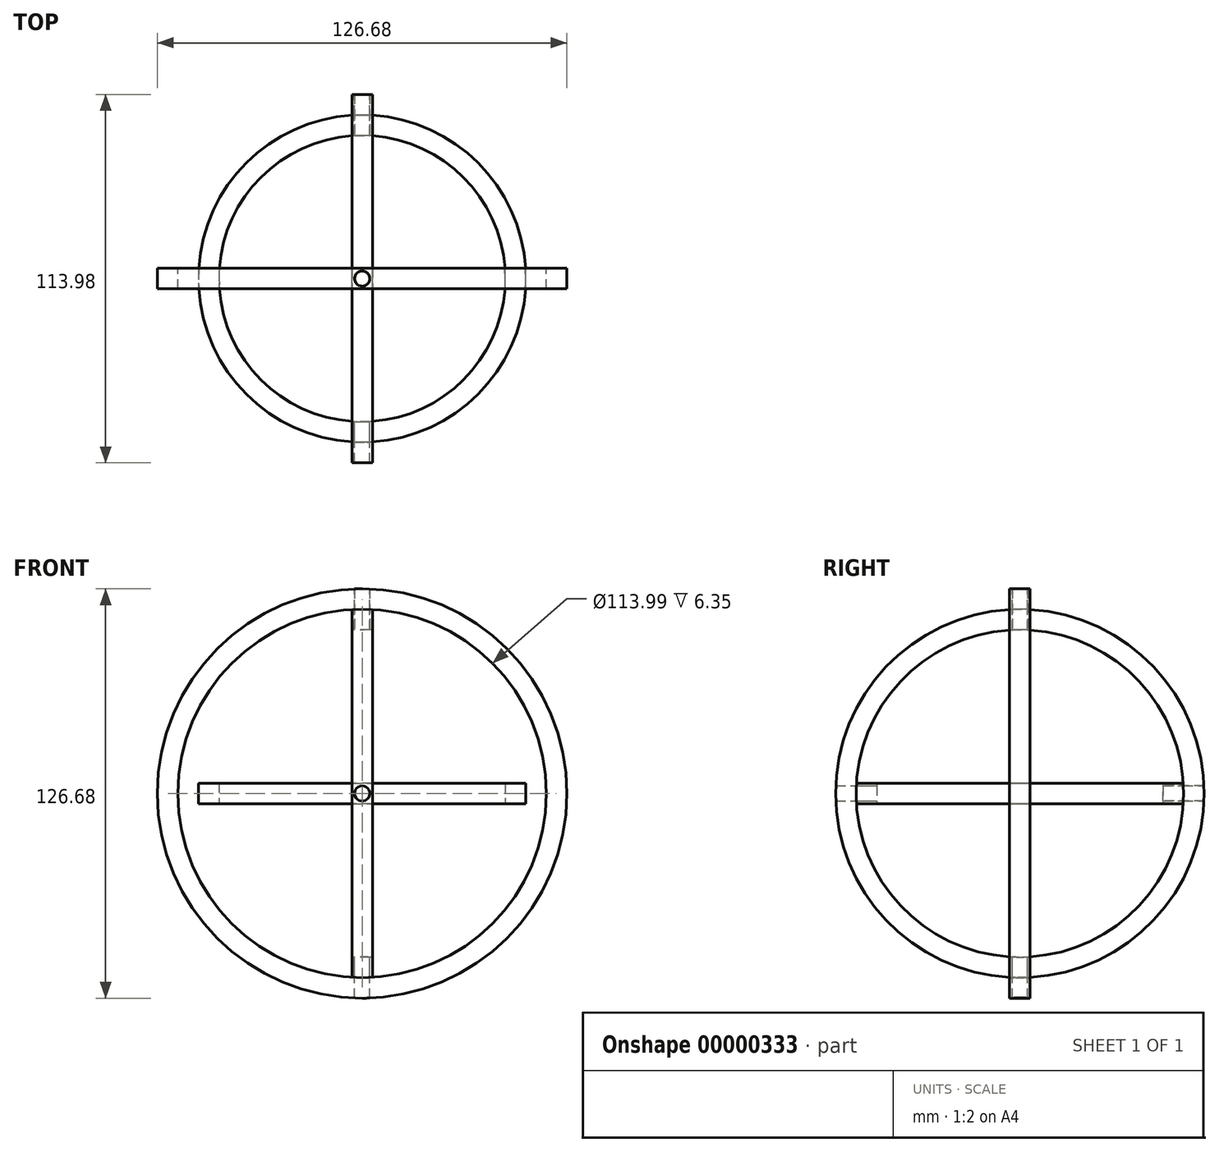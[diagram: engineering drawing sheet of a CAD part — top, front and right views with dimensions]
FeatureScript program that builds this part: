
annotation { "Feature Type Name" : "Feature", "Feature Type Description" : "" }
export const myFeature = defineFeature(function(context is Context, id is Id, definition is map)
    precondition{}
    {
        {
            var Q0;
            Q0=qCreatedBy(makeId("Top.planeOp"),FACE);
            var sketch = newSketch(context, id + "F0", { "sketchPlane" : qUnion([Q0])});
            skCircle(sketch, "E0", {"center": v(0, 0) * mm, "radius": 50.64 * mm});
            skCircle(sketch, "E1", {"center": v(0, 0) * mm, "radius": 44.3 * mm});
            skLineSegment(sketch, "E2", {"start": v(-44.3, 0) * mm, "end": v(-50.64, 0) * mm, "construction": true});
            skLineSegment(sketch, "E3", {"start": v(0, 50.64) * mm, "end": v(0, -50.64) * mm, "construction": true});
            skSolve(sketch);
        }
        {
            var Q0;
            Q0=makeQuery(id+"F0.imprint","IMPRINT",FACE,{"disambiguationData":[TD([[makeQuery(id+"F0.imprint","IMPRINT",EDGE,{"derivedFrom":sQuery(id+"F0.wireOp",EDGE,"E0")}),1.0]])]});
            extrude(context, id + "F1", {"entities" : qUnion([Q0]), "depth" : 3.17 * mm, "hasSecondDirection" : true, "secondDirectionOppositeDirection" : true, "secondDirectionDepth" : 3.17 * mm});
        }
        {
            var Q0;
            Q0=qCreatedBy(makeId("Right.planeOp"),FACE);
            var sketch = newSketch(context, id + "F2", { "sketchPlane" : qUnion([Q0])});
            skPoint(sketch, "E4.0", {"position": v(50.64, 0) * mm});
            skCircle(sketch, "E5", {"center": v(0, 0) * mm, "radius": 50.64 * mm});
            skCircle(sketch, "E6", {"center": v(0, 0) * mm, "radius": 57 * mm});
            skLineSegment(sketch, "E7", {"start": v(50.64, 0) * mm, "end": v(57, 0) * mm, "construction": true});
            skLineSegment(sketch, "E8", {"start": v(0, 50.64) * mm, "end": v(0, 57) * mm, "construction": true});
            skSolve(sketch);
        }
        {
            var Q0;
            Q0=makeQuery(id+"F2.imprint","IMPRINT",FACE,{"disambiguationData":[TD([[makeQuery(id+"F2.imprint","IMPRINT",EDGE,{"derivedFrom":sQuery(id+"F2.wireOp",EDGE,"E5")}),-1.0]])]});
            extrude(context, id + "F3", {"entities" : qUnion([Q0]), "depth" : 3.17 * mm, "hasSecondDirection" : true, "secondDirectionOppositeDirection" : true, "secondDirectionDepth" : 3.17 * mm});
        }
        {
            var Q0;
            Q0=qCreatedBy(makeId("Front.planeOp"),FACE);
            var sketch = newSketch(context, id + "F4", { "sketchPlane" : qUnion([Q0])});
            skPoint(sketch, "E9.0", {"position": v(0, 57) * mm});
            skCircle(sketch, "E10", {"center": v(0, 0) * mm, "radius": 57 * mm});
            skCircle(sketch, "E11", {"center": v(0, 0) * mm, "radius": 63.34 * mm});
            skLineSegment(sketch, "E12", {"start": v(0, 57) * mm, "end": v(0, 63.34) * mm, "construction": true});
            skSolve(sketch);
        }
        {
            var Q0;
            Q0 = qSketchRegion(id + "F4", true);
            extrude(context, id + "F5", {"entities" : qUnion([Q0]), "depth" : 3.17 * mm, "hasSecondDirection" : true, "secondDirectionOppositeDirection" : true, "secondDirectionDepth" : 3.17 * mm});
        }
        {
            var Q0;
            Q0=qCreatedBy(makeId("Front.planeOp"),FACE);
            var sketch = newSketch(context, id + "F6", { "sketchPlane" : qUnion([Q0])});
            skCircle(sketch, "E13", {"center": v(0, 0) * mm, "radius": 2.35 * mm});
            skSolve(sketch);
        }
        {
            var Q0;
            Q0=makeQuery(id+"F6.imprint","IMPRINT",FACE,{"disambiguationData":[TD([[makeQuery(id+"F6.imprint","IMPRINT",EDGE,{"derivedFrom":sQuery(id+"F6.wireOp",EDGE,"E13")}),1.0]])]});
            var Q1;
            Q1=sQuery(id+"F6.wireOp",EDGE,"E13");
            extrude(context, id + "F7", {"entities" : qUnion([Q0]), "operationType" : NewBodyOperationType.REMOVE, "surfaceEntities" : qUnion([Q1]), "endBound" : BoundingType.THROUGH_ALL, "depth" : 25.4 * mm, "hasSecondDirection" : true, "secondDirectionBound" : SecondDirectionBoundingType.THROUGH_ALL, "secondDirectionOppositeDirection" : true, "secondDirectionDepth" : 25.4 * mm});
        }
        {
            var Q0;
            Q0=qCreatedBy(makeId("Top.planeOp"),FACE);
            var sketch = newSketch(context, id + "F8", { "sketchPlane" : qUnion([Q0])});
            skCircle(sketch, "E14", {"center": v(0, 0) * mm, "radius": 2.35 * mm});
            skSolve(sketch);
        }
        {
            var Q0;
            Q0 = qSketchRegion(id + "F8", true);
            extrude(context, id + "F9", {"entities" : qUnion([Q0]), "operationType" : NewBodyOperationType.REMOVE, "endBound" : BoundingType.THROUGH_ALL, "oppositeDirection" : true, "depth" : 25.4 * mm, "hasSecondDirection" : true, "secondDirectionBound" : SecondDirectionBoundingType.THROUGH_ALL, "secondDirectionOppositeDirection" : false, "secondDirectionDepth" : 25.4 * mm});
        }
        {
            var Q0;
            Q0=makeQuery(id+"F8.imprint","IMPRINT",FACE,{"disambiguationData":[TD([[makeQuery(id+"F8.imprint","IMPRINT",EDGE,{"derivedFrom":sQuery(id+"F8.wireOp",EDGE,"E14")}),1.0]])]});
            var Q1;
            Q1=sQuery(id+"F8.wireOp",EDGE,"E14");
            var Q2;
            Q2=makeQuery(id+"F5.opExtrude","SWEPT_FACE",FACE,{"disambiguationData":[OSD([sQuery(id+"F4.wireOp",EDGE,"E11")])]});
            var Q3;
            Q3=makeQuery(id+"F3.opExtrude","SWEPT_FACE",FACE,{"disambiguationData":[OSD([sQuery(id+"F2.wireOp",EDGE,"E5")])]});
            extrude(context, id + "F10", {"entities" : qUnion([Q0]), "surfaceEntities" : qUnion([Q1]), "endBound" : BoundingType.UP_TO_SURFACE, "endBoundEntityFace" : qUnion([Q2]), "depth" : 25.4 * mm, "hasSecondDirection" : true, "secondDirectionBound" : SecondDirectionBoundingType.UP_TO_SURFACE, "secondDirectionOppositeDirection" : false, "secondDirectionBoundEntityFace" : qUnion([Q3]), "secondDirectionDepth" : 25.4 * mm});
        }
        {
            var Q0;
            Q0 = qSketchRegion(id + "F8", true);
            var Q1;
            Q1=sQuery(id+"F8.wireOp",EDGE,"E14");
            var Q2;
            Q2=makeQuery(id+"F5.opExtrude","SWEPT_FACE",FACE,{"disambiguationData":[OSD([sQuery(id+"F4.wireOp",EDGE,"E11")])]});
            var Q3;
            Q3=makeQuery(id+"F3.opExtrude","SWEPT_FACE",FACE,{"disambiguationData":[OSD([sQuery(id+"F2.wireOp",EDGE,"E5")])]});
            extrude(context, id + "F11", {"entities" : qUnion([Q0]), "surfaceEntities" : qUnion([Q1]), "endBound" : BoundingType.UP_TO_SURFACE, "oppositeDirection" : true, "endBoundEntityFace" : qUnion([Q2]), "depth" : 25.4 * mm, "hasSecondDirection" : true, "secondDirectionBound" : SecondDirectionBoundingType.UP_TO_SURFACE, "secondDirectionOppositeDirection" : true, "secondDirectionBoundEntityFace" : qUnion([Q3]), "secondDirectionDepth" : 25.4 * mm});
        }
        {
            var Q0;
            Q0 = qSketchRegion(id + "F6", true);
            var Q1;
            Q1=makeQuery(id+"F3.opExtrude","SWEPT_FACE",FACE,{"disambiguationData":[OSD([sQuery(id+"F2.wireOp",EDGE,"E6")])]});
            var Q2;
            Q2=makeQuery(id+"F1.opExtrude","SWEPT_FACE",FACE,{"disambiguationData":[OSD([sQuery(id+"F0.wireOp",EDGE,"E1")])]});
            extrude(context, id + "F12", {"entities" : qUnion([Q0]), "endBound" : BoundingType.UP_TO_SURFACE, "oppositeDirection" : true, "endBoundEntityFace" : qUnion([Q1]), "depth" : 25.4 * mm, "hasSecondDirection" : true, "secondDirectionBound" : SecondDirectionBoundingType.UP_TO_SURFACE, "secondDirectionOppositeDirection" : true, "secondDirectionBoundEntityFace" : qUnion([Q2]), "secondDirectionDepth" : 25.4 * mm});
        }
        {
            var Q0;
            Q0=makeQuery(id+"F6.imprint","IMPRINT",FACE,{"disambiguationData":[TD([[makeQuery(id+"F6.imprint","IMPRINT",EDGE,{"derivedFrom":sQuery(id+"F6.wireOp",EDGE,"E13")}),1.0]])]});
            var Q1;
            Q1=makeQuery(id+"F3.opExtrude","SWEPT_FACE",FACE,{"disambiguationData":[OSD([sQuery(id+"F2.wireOp",EDGE,"E6")])]});
            var Q2;
            Q2=makeQuery(id+"F1.opExtrude","SWEPT_FACE",FACE,{"disambiguationData":[OSD([sQuery(id+"F0.wireOp",EDGE,"E1")])]});
            extrude(context, id + "F13", {"entities" : qUnion([Q0]), "endBound" : BoundingType.UP_TO_SURFACE, "endBoundEntityFace" : qUnion([Q1]), "depth" : 25.4 * mm, "hasSecondDirection" : true, "secondDirectionBound" : SecondDirectionBoundingType.UP_TO_SURFACE, "secondDirectionOppositeDirection" : false, "secondDirectionBoundEntityFace" : qUnion([Q2]), "secondDirectionDepth" : 25.4 * mm});
        }
    });
